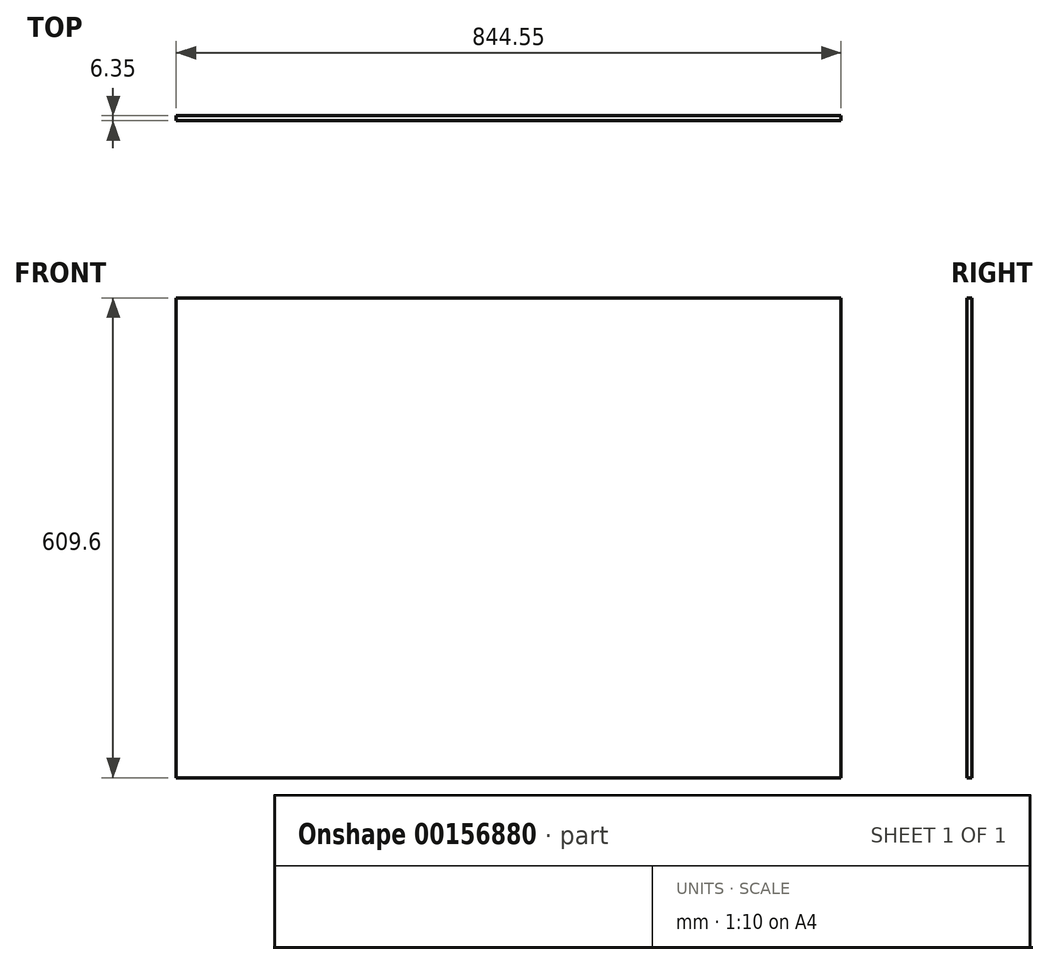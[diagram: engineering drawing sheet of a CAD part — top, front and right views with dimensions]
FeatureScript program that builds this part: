
annotation { "Feature Type Name" : "Feature", "Feature Type Description" : "" }
export const myFeature = defineFeature(function(context is Context, id is Id, definition is map)
    precondition{}
    {
        {
            var Q0;
            Q0=qCreatedBy(makeId("Front.planeOp"),FACE);
            var sketch = newSketch(context, id + "F0", { "sketchPlane" : qUnion([Q0])});
            skLineSegment(sketch, "E0.bottom", {"start": v(0, 0) * mm, "end": v(844.55, 0) * mm});
            skLineSegment(sketch, "E0.top", {"start": v(0, 609.6) * mm, "end": v(844.55, 609.6) * mm});
            skLineSegment(sketch, "E0.left", {"start": v(0, 0) * mm, "end": v(0, 609.6) * mm});
            skLineSegment(sketch, "E0.right", {"start": v(844.55, 0) * mm, "end": v(844.55, 609.6) * mm});
            skSolve(sketch);
        }
        {
            var Q0;
            Q0 = qSketchRegion(id + "F0", true);
            extrude(context, id + "F1", {"entities" : qUnion([Q0]), "depth" : 6.35 * mm});
        }
    });
